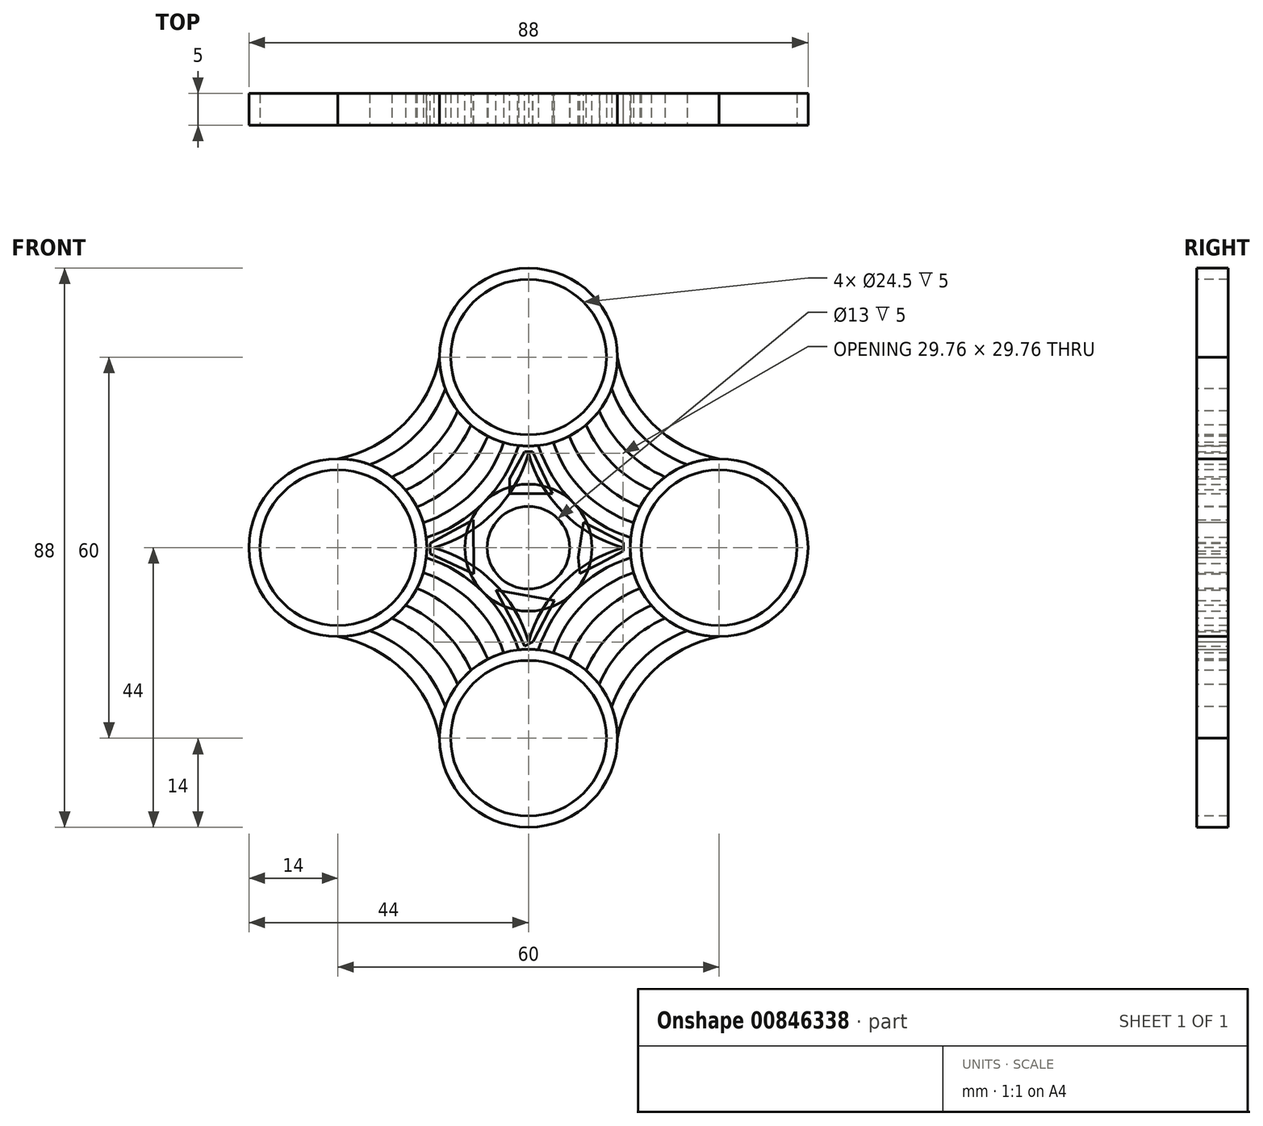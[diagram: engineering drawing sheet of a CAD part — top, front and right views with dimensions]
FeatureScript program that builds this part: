
annotation { "Feature Type Name" : "Feature", "Feature Type Description" : "" }
export const myFeature = defineFeature(function(context is Context, id is Id, definition is map)
    precondition{}
    {
        {
            var Q0;
            Q0=qCreatedBy(makeId("Front.planeOp"),FACE);
            var sketch = newSketch(context, id + "F0", { "sketchPlane" : qUnion([Q0])});
            skCircle(sketch, "E0", {"center": v(0, 0) * mm, "radius": 10 * mm});
            skSolve(sketch);
        }
        {
            var Q0;
            Q0 = qSketchRegion(id + "F0", true);
            extrude(context, id + "F1", {"entities" : qUnion([Q0]), "depth" : 5 * mm, "offsetDistance" : 25 * mm});
        }
        {
            var Q0;
            Q0=makeQuery(id+"F1.opExtrude","CAP_FACE",FACE,{"disambiguationData":[OSD([sQuery(id+"F0.wireOp",EDGE,"E0")])],"isStart":false});
            var sketch = newSketch(context, id + "F2", { "sketchPlane" : qUnion([Q0])});
            skCircle(sketch, "E1", {"center": v(0, 0) * mm, "radius": 6.5 * mm});
            skSolve(sketch);
        }
        {
            var Q0;
            Q0 = qSketchRegion(id + "F2", true);
            extrude(context, id + "F3", {"entities" : qUnion([Q0]), "operationType" : NewBodyOperationType.REMOVE, "oppositeDirection" : true, "depth" : 5 * mm, "offsetDistance" : 25 * mm});
        }
        {
            var Q0;
            Q0=qCreatedBy(makeId("Front.planeOp"),FACE);
            var sketch = newSketch(context, id + "F4", { "sketchPlane" : qUnion([Q0])});
            skCircle(sketch, "E2", {"center": v(0, 30) * mm, "radius": 14 * mm});
            skCircle(sketch, "E3.1.0", {"center": v(-30, 0) * mm, "radius": 14 * mm});
            skCircle(sketch, "E3.2.0", {"center": v(0, -30) * mm, "radius": 14 * mm});
            skCircle(sketch, "E3.3.0", {"center": v(30, 0) * mm, "radius": 14 * mm});
            skPoint(sketch, "E3.center", {"position": v(0, 0) * mm});
            skSolve(sketch);
        }
        {
            var Q0;
            Q0 = qSketchRegion(id + "F4", true);
            extrude(context, id + "F5", {"entities" : qUnion([Q0]), "depth" : 5 * mm, "offsetDistance" : 25 * mm});
        }
        {
            var Q0;
            Q0=makeQuery(id+"F5.opExtrude","CAP_FACE",FACE,{"disambiguationData":[OSD([sQuery(id+"F4.wireOp",EDGE,"E2")])],"isStart":false});
            var sketch = newSketch(context, id + "F6", { "sketchPlane" : qUnion([Q0])});
            skCircle(sketch, "E4", {"center": v(0, 30) * mm, "radius": 12.25 * mm});
            skCircle(sketch, "E5.1.0", {"center": v(-30, 0) * mm, "radius": 12.25 * mm});
            skCircle(sketch, "E5.2.0", {"center": v(0, -30) * mm, "radius": 12.25 * mm});
            skCircle(sketch, "E5.3.0", {"center": v(30, 0) * mm, "radius": 12.25 * mm});
            skPoint(sketch, "E5.center", {"position": v(0, 0) * mm});
            skSolve(sketch);
        }
        {
            var Q0;
            Q0 = qSketchRegion(id + "F6", true);
            extrude(context, id + "F7", {"entities" : qUnion([Q0]), "operationType" : NewBodyOperationType.REMOVE, "oppositeDirection" : true, "depth" : 5 * mm, "offsetDistance" : 25 * mm});
        }
        {
            var Q0;
            Q0=makeQuery(id+"F5.opExtrude","CAP_FACE",FACE,{"disambiguationData":[OSD([sQuery(id+"F4.wireOp",EDGE,"E3.1.0")])],"isStart":false});
            var sketch = newSketch(context, id + "F8", { "sketchPlane" : qUnion([Q0])});
            skArc(sketch, "E6", {"start": v(-30, 14) * mm, "mid": v(-19.52, 19.52) * mm, "end": v(-14, 30) * mm});
            skArc(sketch, "E7", {"start": v(-16, -0.29) * mm, "mid": v(-5.5, 5.5) * mm, "end": v(0.29, 16) * mm});
            skLineSegment(sketch, "E8", {"start": v(0, 0) * mm, "end": v(-30, 30) * mm, "construction": true});
            skArc(sketch, "E9", {"start": v(-14, 30) * mm, "mid": v(-9.8, 20) * mm, "end": v(0.29, 16) * mm});
            skArc(sketch, "E10", {"start": v(-16, -0.29) * mm, "mid": v(-20, 9.8) * mm, "end": v(-30, 14) * mm});
            skArc(sketch, "E11.1.0", {"start": v(0.29, -16) * mm, "mid": v(-9.8, -20) * mm, "end": v(-14, -30) * mm});
            skArc(sketch, "E11.1.1", {"start": v(0.29, -16) * mm, "mid": v(-5.5, -5.5) * mm, "end": v(-16, 0.29) * mm});
            skLineSegment(sketch, "E11.1.2", {"start": v(0, 0) * mm, "end": v(-30, -30) * mm, "construction": true});
            skArc(sketch, "E11.1.3", {"start": v(-14, -30) * mm, "mid": v(-19.52, -19.52) * mm, "end": v(-30, -14) * mm});
            skArc(sketch, "E11.1.4", {"start": v(-30, -14) * mm, "mid": v(-20, -9.8) * mm, "end": v(-16, 0.29) * mm});
            skArc(sketch, "E11.2.0", {"start": v(16, 0.29) * mm, "mid": v(20, -9.8) * mm, "end": v(30, -14) * mm});
            skArc(sketch, "E11.2.1", {"start": v(16, 0.29) * mm, "mid": v(5.5, -5.5) * mm, "end": v(-0.29, -16) * mm});
            skLineSegment(sketch, "E11.2.2", {"start": v(0, 0) * mm, "end": v(30, -30) * mm, "construction": true});
            skArc(sketch, "E11.2.3", {"start": v(30, -14) * mm, "mid": v(19.52, -19.52) * mm, "end": v(14, -30) * mm});
            skArc(sketch, "E11.2.4", {"start": v(14, -30) * mm, "mid": v(9.8, -20) * mm, "end": v(-0.29, -16) * mm});
            skArc(sketch, "E11.3.0", {"start": v(-0.29, 16) * mm, "mid": v(9.8, 20) * mm, "end": v(14, 30) * mm});
            skArc(sketch, "E11.3.1", {"start": v(-0.29, 16) * mm, "mid": v(5.5, 5.5) * mm, "end": v(16, -0.29) * mm});
            skLineSegment(sketch, "E11.3.2", {"start": v(0, 0) * mm, "end": v(30, 30) * mm, "construction": true});
            skArc(sketch, "E11.3.3", {"start": v(14, 30) * mm, "mid": v(19.52, 19.52) * mm, "end": v(30, 14) * mm});
            skArc(sketch, "E11.3.4", {"start": v(30, 14) * mm, "mid": v(20, 9.8) * mm, "end": v(16, -0.29) * mm});
            skPoint(sketch, "E11.center", {"position": v(0, 0) * mm});
            skSolve(sketch);
        }
        {
            var Q0;
            Q0 = qSketchRegion(id + "F8", true);
            var Q1;
            Q1 = qSketchRegion(id + "F10", true);
            extrude(context, id + "F9", {"entities" : qUnion([Q0, Q1]), "oppositeDirection" : true, "depth" : 5 * mm, "offsetDistance" : 25 * mm});
        }
        {
            var Q0;
            Q0=makeQuery(id+"F9.opExtrude","CAP_FACE",FACE,{"disambiguationData":[OSD([sQuery(id+"F8.wireOp",EDGE,"E6"),sQuery(id+"F8.wireOp",EDGE,"E7"),sQuery(id+"F8.wireOp",EDGE,"E9"),sQuery(id+"F8.wireOp",EDGE,"E10"),sQuery(id+"F8.wireOp",EDGE,"E11.1.0"),sQuery(id+"F8.wireOp",EDGE,"E11.1.1"),sQuery(id+"F8.wireOp",EDGE,"E11.1.3"),sQuery(id+"F8.wireOp",EDGE,"E11.1.4"),sQuery(id+"F8.wireOp",EDGE,"E11.2.0"),sQuery(id+"F8.wireOp",EDGE,"E11.2.1"),sQuery(id+"F8.wireOp",EDGE,"E11.2.3"),sQuery(id+"F8.wireOp",EDGE,"E11.2.4"),sQuery(id+"F8.wireOp",EDGE,"E11.3.0"),sQuery(id+"F8.wireOp",EDGE,"E11.3.1"),sQuery(id+"F8.wireOp",EDGE,"E11.3.3"),sQuery(id+"F8.wireOp",EDGE,"E11.3.4")])],"isStart":true});
            var sketch = newSketch(context, id + "F10", { "sketchPlane" : qUnion([Q0])});
            skArc(sketch, "E12", {"start": v(-25, 13.08) * mm, "mid": v(-17.72, 17.72) * mm, "end": v(-13.08, 25) * mm});
            skArc(sketch, "E13", {"start": v(-21.5, 11.13) * mm, "mid": v(-15.33, 15.33) * mm, "end": v(-11.13, 21.5) * mm});
            skArc(sketch, "E14", {"start": v(-13.08, 25) * mm, "mid": v(-12.23, 23.18) * mm, "end": v(-11.13, 21.5) * mm});
            skArc(sketch, "E15", {"start": v(-21.5, 11.13) * mm, "mid": v(-23.18, 12.23) * mm, "end": v(-25, 13.08) * mm});
            skArc(sketch, "E16", {"start": v(-19.33, 9.06) * mm, "mid": v(-13.23, 13.23) * mm, "end": v(-9.06, 19.33) * mm});
            skLineSegment(sketch, "E17", {"start": v(0, 0) * mm, "end": v(-31.86, 31.86) * mm, "construction": true});
            skArc(sketch, "E18", {"start": v(-17.56, 6.42) * mm, "mid": v(-10.84, 10.84) * mm, "end": v(-6.42, 17.56) * mm});
            skArc(sketch, "E19", {"start": v(-9.06, 19.33) * mm, "mid": v(-7.8, 18.37) * mm, "end": v(-6.42, 17.56) * mm});
            skArc(sketch, "E20", {"start": v(-17.56, 6.42) * mm, "mid": v(-18.37, 7.8) * mm, "end": v(-19.33, 9.06) * mm});
            skArc(sketch, "E21", {"start": v(-16.56, 3.91) * mm, "mid": v(-8.74, 8.74) * mm, "end": v(-3.91, 16.56) * mm});
            skArc(sketch, "E22", {"start": v(-16.09, 1.57) * mm, "mid": v(-7.07, 7.07) * mm, "end": v(-1.57, 16.09) * mm});
            skArc(sketch, "E23", {"start": v(-16.09, 1.57) * mm, "mid": v(-16.27, 2.75) * mm, "end": v(-16.56, 3.91) * mm});
            skArc(sketch, "E24", {"start": v(-3.91, 16.56) * mm, "mid": v(-2.75, 16.27) * mm, "end": v(-1.57, 16.09) * mm});
            skArc(sketch, "E25.1.0", {"start": v(-11.13, -21.5) * mm, "mid": v(-15.33, -15.33) * mm, "end": v(-21.5, -11.13) * mm});
            skArc(sketch, "E25.1.1", {"start": v(-13.08, -25) * mm, "mid": v(-17.72, -17.72) * mm, "end": v(-25, -13.08) * mm});
            skLineSegment(sketch, "E25.1.2", {"start": v(0, 0) * mm, "end": v(-31.86, -31.86) * mm, "construction": true});
            skArc(sketch, "E25.1.3", {"start": v(-1.57, -16.09) * mm, "mid": v(-7.07, -7.07) * mm, "end": v(-16.09, -1.57) * mm});
            skArc(sketch, "E25.1.4", {"start": v(-6.42, -17.56) * mm, "mid": v(-10.84, -10.84) * mm, "end": v(-17.56, -6.42) * mm});
            skArc(sketch, "E25.1.5", {"start": v(-3.91, -16.56) * mm, "mid": v(-8.74, -8.74) * mm, "end": v(-16.56, -3.91) * mm});
            skArc(sketch, "E25.1.6", {"start": v(-9.06, -19.33) * mm, "mid": v(-13.23, -13.23) * mm, "end": v(-19.33, -9.06) * mm});
            skArc(sketch, "E25.1.7", {"start": v(-1.57, -16.09) * mm, "mid": v(-2.75, -16.27) * mm, "end": v(-3.91, -16.56) * mm});
            skArc(sketch, "E25.1.8", {"start": v(-6.42, -17.56) * mm, "mid": v(-7.8, -18.37) * mm, "end": v(-9.06, -19.33) * mm});
            skArc(sketch, "E25.1.9", {"start": v(-25, -13.08) * mm, "mid": v(-23.18, -12.23) * mm, "end": v(-21.5, -11.13) * mm});
            skArc(sketch, "E25.1.10", {"start": v(-16.56, -3.91) * mm, "mid": v(-16.27, -2.75) * mm, "end": v(-16.09, -1.57) * mm});
            skArc(sketch, "E25.1.11", {"start": v(-11.13, -21.5) * mm, "mid": v(-12.23, -23.18) * mm, "end": v(-13.08, -25) * mm});
            skArc(sketch, "E25.1.12", {"start": v(-19.33, -9.06) * mm, "mid": v(-18.37, -7.8) * mm, "end": v(-17.56, -6.42) * mm});
            skArc(sketch, "E25.2.0", {"start": v(21.5, -11.13) * mm, "mid": v(15.33, -15.33) * mm, "end": v(11.13, -21.5) * mm});
            skArc(sketch, "E25.2.1", {"start": v(25, -13.08) * mm, "mid": v(17.72, -17.72) * mm, "end": v(13.08, -25) * mm});
            skLineSegment(sketch, "E25.2.2", {"start": v(0, 0) * mm, "end": v(31.86, -31.86) * mm, "construction": true});
            skArc(sketch, "E25.2.3", {"start": v(16.09, -1.57) * mm, "mid": v(7.07, -7.07) * mm, "end": v(1.57, -16.09) * mm});
            skArc(sketch, "E25.2.4", {"start": v(17.56, -6.42) * mm, "mid": v(10.84, -10.84) * mm, "end": v(6.42, -17.56) * mm});
            skArc(sketch, "E25.2.5", {"start": v(16.56, -3.91) * mm, "mid": v(8.74, -8.74) * mm, "end": v(3.91, -16.56) * mm});
            skArc(sketch, "E25.2.6", {"start": v(19.33, -9.06) * mm, "mid": v(13.23, -13.23) * mm, "end": v(9.06, -19.33) * mm});
            skArc(sketch, "E25.2.7", {"start": v(16.09, -1.57) * mm, "mid": v(16.27, -2.75) * mm, "end": v(16.56, -3.91) * mm});
            skArc(sketch, "E25.2.8", {"start": v(17.56, -6.42) * mm, "mid": v(18.37, -7.8) * mm, "end": v(19.33, -9.06) * mm});
            skArc(sketch, "E25.2.9", {"start": v(13.08, -25) * mm, "mid": v(12.23, -23.18) * mm, "end": v(11.13, -21.5) * mm});
            skArc(sketch, "E25.2.10", {"start": v(3.91, -16.56) * mm, "mid": v(2.75, -16.27) * mm, "end": v(1.57, -16.09) * mm});
            skArc(sketch, "E25.2.11", {"start": v(21.5, -11.13) * mm, "mid": v(23.18, -12.23) * mm, "end": v(25, -13.08) * mm});
            skArc(sketch, "E25.2.12", {"start": v(9.06, -19.33) * mm, "mid": v(7.8, -18.37) * mm, "end": v(6.42, -17.56) * mm});
            skArc(sketch, "E25.3.0", {"start": v(11.13, 21.5) * mm, "mid": v(15.33, 15.33) * mm, "end": v(21.5, 11.13) * mm});
            skArc(sketch, "E25.3.1", {"start": v(13.08, 25) * mm, "mid": v(17.72, 17.72) * mm, "end": v(25, 13.08) * mm});
            skLineSegment(sketch, "E25.3.2", {"start": v(0, 0) * mm, "end": v(31.86, 31.86) * mm, "construction": true});
            skArc(sketch, "E25.3.3", {"start": v(1.57, 16.09) * mm, "mid": v(7.07, 7.07) * mm, "end": v(16.09, 1.57) * mm});
            skArc(sketch, "E25.3.4", {"start": v(6.42, 17.56) * mm, "mid": v(10.84, 10.84) * mm, "end": v(17.56, 6.42) * mm});
            skArc(sketch, "E25.3.5", {"start": v(3.91, 16.56) * mm, "mid": v(8.74, 8.74) * mm, "end": v(16.56, 3.91) * mm});
            skArc(sketch, "E25.3.6", {"start": v(9.06, 19.33) * mm, "mid": v(13.23, 13.23) * mm, "end": v(19.33, 9.06) * mm});
            skArc(sketch, "E25.3.7", {"start": v(1.57, 16.09) * mm, "mid": v(2.75, 16.27) * mm, "end": v(3.91, 16.56) * mm});
            skArc(sketch, "E25.3.8", {"start": v(6.42, 17.56) * mm, "mid": v(7.8, 18.37) * mm, "end": v(9.06, 19.33) * mm});
            skArc(sketch, "E25.3.9", {"start": v(25, 13.08) * mm, "mid": v(23.18, 12.23) * mm, "end": v(21.5, 11.13) * mm});
            skArc(sketch, "E25.3.10", {"start": v(16.56, 3.91) * mm, "mid": v(16.27, 2.75) * mm, "end": v(16.09, 1.57) * mm});
            skArc(sketch, "E25.3.11", {"start": v(11.13, 21.5) * mm, "mid": v(12.23, 23.18) * mm, "end": v(13.08, 25) * mm});
            skArc(sketch, "E25.3.12", {"start": v(19.33, 9.06) * mm, "mid": v(18.37, 7.8) * mm, "end": v(17.56, 6.42) * mm});
            skPoint(sketch, "E25.center", {"position": v(0, 0) * mm});
            skSolve(sketch);
        }
        {
            var Q0;
            Q0 = qSketchRegion(id + "F10", true);
            extrude(context, id + "F11", {"entities" : qUnion([Q0]), "operationType" : NewBodyOperationType.REMOVE, "oppositeDirection" : true, "depth" : 5 * mm, "offsetDistance" : 25 * mm});
        }
        {
            var Q0;
            Q0=makeQuery(id+"F1.opExtrude","CAP_FACE",FACE,{"disambiguationData":[OSD([sQuery(id+"F0.wireOp",EDGE,"E0")])],"isStart":true});
            var sketch = newSketch(context, id + "F12", { "sketchPlane" : qUnion([Q0])});
            skLineSegment(sketch, "E26", {"start": v(-8.65, 4) * mm, "end": v(-14.97, 0.84) * mm});
            skLineSegment(sketch, "E27", {"start": v(-14.97, 0.84) * mm, "end": v(-14.97, -0.5) * mm});
            skLineSegment(sketch, "E28", {"start": v(-14.97, -0.5) * mm, "end": v(-11.26, -2.45) * mm});
            skLineSegment(sketch, "E29", {"start": v(-11.26, -2.45) * mm, "end": v(-8.1, -4.03) * mm});
            skLineSegment(sketch, "E30", {"start": v(-8.1, -4.03) * mm, "end": v(-7.83, -1.5) * mm});
            skLineSegment(sketch, "E31", {"start": v(-7.83, -1.5) * mm, "end": v(-8.65, 4) * mm});
            skLineSegment(sketch, "E32", {"start": v(-3.78, 8.53) * mm, "end": v(2.95, 8.53) * mm});
            skLineSegment(sketch, "E33", {"start": v(2.95, 8.53) * mm, "end": v(2.95, 10.87) * mm});
            skLineSegment(sketch, "E34", {"start": v(2.95, 10.87) * mm, "end": v(0.62, 15.12) * mm});
            skLineSegment(sketch, "E35", {"start": v(0.62, 15.12) * mm, "end": v(-0.69, 15.12) * mm});
            skLineSegment(sketch, "E36", {"start": v(-0.69, 15.12) * mm, "end": v(-3.78, 8.53) * mm});
            skLineSegment(sketch, "E37", {"start": v(8.65, 4.41) * mm, "end": v(15.45, 0.7) * mm});
            skLineSegment(sketch, "E38", {"start": v(15.45, 0.7) * mm, "end": v(15.45, -0.94) * mm});
            skLineSegment(sketch, "E39", {"start": v(15.45, -0.94) * mm, "end": v(8.58, -4.1) * mm});
            skLineSegment(sketch, "E40", {"start": v(8.58, -4.1) * mm, "end": v(8.65, 4.41) * mm});
            skLineSegment(sketch, "E41", {"start": v(5.12, -6.64) * mm, "end": v(-4.09, -8.32) * mm});
            skLineSegment(sketch, "E42", {"start": v(-4.09, -8.32) * mm, "end": v(-0.72, -14.81) * mm});
            skLineSegment(sketch, "E43", {"start": v(-0.72, -14.81) * mm, "end": v(0.58, -15.47) * mm});
            skLineSegment(sketch, "E44", {"start": v(0.58, -15.47) * mm, "end": v(1.71, -13.21) * mm});
            skLineSegment(sketch, "E45", {"start": v(1.71, -13.21) * mm, "end": v(5.12, -6.64) * mm});
            skSolve(sketch);
        }
        {
            var Q0;
            Q0 = qSketchRegion(id + "F12", true);
            extrude(context, id + "F13", {"entities" : qUnion([Q0]), "oppositeDirection" : true, "depth" : 5 * mm, "offsetDistance" : 25 * mm});
        }
    });
